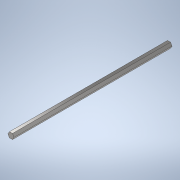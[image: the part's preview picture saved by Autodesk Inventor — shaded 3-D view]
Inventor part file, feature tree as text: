
AUTODESK INVENTOR PART (.ipt)
format: ipt  version: 2020 (Build 240168000, 168)  size: 103,424 bytes
history: native  units: in
note: dims shown in document units (in); Inventor stores cm internally (conversion verified against a paired STEP export)
features: extrude x1, sketch x1
ambient origin geometry x8: Origin, YZ Plane, XZ Plane, XY Plane, X Axis, Y Axis, Z Axis, Center Point
bodies: Solid1 (feature_tree)
feature tree (2):
  extrude  "Extrusion1"  Depth=15.0in TaperAngle=0.0deg
  sketch  "Sketch1"  dims[d0=0.5in d1=15.0in d2=0.0in]
